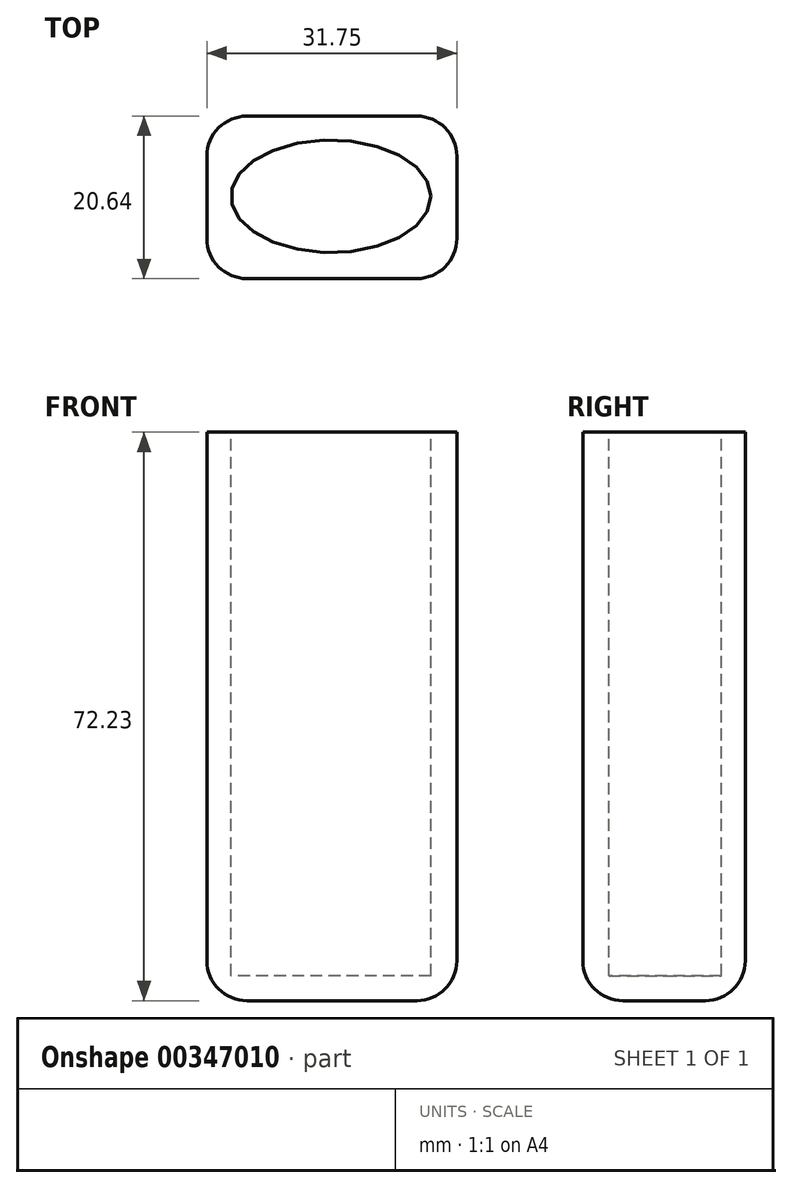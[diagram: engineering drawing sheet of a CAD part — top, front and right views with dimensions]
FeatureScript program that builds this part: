
annotation { "Feature Type Name" : "Feature", "Feature Type Description" : "" }
export const myFeature = defineFeature(function(context is Context, id is Id, definition is map)
    precondition{}
    {
        {
            var Q0;
            Q0=qCreatedBy(makeId("Top.planeOp"),FACE);
            var sketch = newSketch(context, id + "F0", { "sketchPlane" : qUnion([Q0])});
            skLineSegment(sketch, "E0.bottom", {"start": v(-12.58, 7.01) * mm, "end": v(12.82, 7.01) * mm});
            skLineSegment(sketch, "E0.top", {"start": v(-12.58, -7.27) * mm, "end": v(12.82, -7.27) * mm});
            skLineSegment(sketch, "E0.left", {"start": v(-12.58, 7.01) * mm, "end": v(-12.58, -7.27) * mm});
            skLineSegment(sketch, "E0.right", {"start": v(12.82, 7.01) * mm, "end": v(12.82, -7.27) * mm});
            skSolve(sketch);
        }
        {
            var Q0;
            Q0 = qSketchRegion(id + "F0", true);
            extrude(context, id + "F1", {"entities" : qUnion([Q0]), "depth" : 69.06 * mm});
        }
        {
            var Q0;
            Q0=makeQuery(id+"F1.opExtrude","SWEPT_FACE",FACE,{"disambiguationData":[OSD([sQuery(id+"F0.wireOp",EDGE,"E0.top")])]});
            extrude(context, id + "F2", {"entities" : qUnion([Q0]), "operationType" : NewBodyOperationType.ADD, "depth" : 3.17 * mm});
        }
        {
            var Q0;
            {var subQ0=sQuery(id+"F0.wireOp",EDGE,"E0.left");Q0=makeQuery(id+"F2.boolean.opBoolean","MERGE",FACE,{"derivedFrom":[makeQuery(id+"F1.opExtrude","SWEPT_FACE",FACE,{"disambiguationData":[OSD([subQ0])]}),makeQuery(id+"F2.opExtrude","SWEPT_FACE",FACE,{"disambiguationData":[OSD([sQuery(id+"F0.wireOp",EDGE,"E0.top"),subQ0])]})]});}
            extrude(context, id + "F3", {"entities" : qUnion([Q0]), "operationType" : NewBodyOperationType.ADD, "depth" : 3.17 * mm});
        }
        {
            var Q0;
            {var subQ0=sQuery(id+"F0.wireOp",EDGE,"E0.bottom");Q0=makeQuery(id+"F3.boolean.opBoolean","MERGE",FACE,{"derivedFrom":[makeQuery(id+"F1.opExtrude","SWEPT_FACE",FACE,{"disambiguationData":[OSD([subQ0])]}),makeQuery(id+"F3.opExtrude","SWEPT_FACE",FACE,{"disambiguationData":[OSD([subQ0,sQuery(id+"F0.wireOp",EDGE,"E0.left")])]})]});}
            extrude(context, id + "F4", {"entities" : qUnion([Q0]), "operationType" : NewBodyOperationType.ADD, "depth" : 3.17 * mm});
        }
        {
            var Q0;
            {var subQ0=sQuery(id+"F0.wireOp",EDGE,"E0.right");Q0=makeQuery(id+"F4.boolean.opBoolean","MERGE",FACE,{"derivedFrom":[makeQuery(id+"F2.boolean.opBoolean","MERGE",FACE,{"derivedFrom":[makeQuery(id+"F1.opExtrude","SWEPT_FACE",FACE,{"disambiguationData":[OSD([subQ0])]}),makeQuery(id+"F2.opExtrude","SWEPT_FACE",FACE,{"disambiguationData":[OSD([sQuery(id+"F0.wireOp",EDGE,"E0.top"),subQ0])]})]}),makeQuery(id+"F4.opExtrude","SWEPT_FACE",FACE,{"disambiguationData":[OSD([sQuery(id+"F0.wireOp",EDGE,"E0.bottom"),subQ0])]})]});}
            extrude(context, id + "F5", {"entities" : qUnion([Q0]), "operationType" : NewBodyOperationType.ADD, "depth" : 3.17 * mm});
        }
        {
            var Q0;
            {var subQ0=sQuery(id+"F0.wireOp",EDGE,"E0.right");var subQ1=sQuery(id+"F0.wireOp",EDGE,"E0.bottom");var subQ2=sQuery(id+"F0.wireOp",EDGE,"E0.top");var subQ3=sQuery(id+"F0.wireOp",EDGE,"E0.left");Q0=makeQuery(id+"F5.boolean.opBoolean","MERGE",FACE,{"derivedFrom":[makeQuery(id+"F4.boolean.opBoolean","MERGE",FACE,{"derivedFrom":[makeQuery(id+"F3.boolean.opBoolean","MERGE",FACE,{"derivedFrom":[makeQuery(id+"F2.boolean.opBoolean","MERGE",FACE,{"derivedFrom":[makeQuery(id+"F1.opExtrude","CAP_FACE",FACE,{"disambiguationData":[OSD([subQ1,subQ2,subQ3,subQ0])],"isStart":false}),makeQuery(id+"F2.opExtrude","SWEPT_FACE",FACE,{"disambiguationData":[OSD([subQ2]),TDD([makeQuery(id+"F1.opExtrude","CAP_EDGE",EDGE,{"disambiguationData":[OSD([subQ2])],"isStart":false})])]})]}),makeQuery(id+"F3.opExtrude","SWEPT_FACE",FACE,{"disambiguationData":[OSD([subQ2,subQ3]),TDD([makeQuery(id+"F2.boolean.opBoolean","MERGE",EDGE,{"derivedFrom":[makeQuery(id+"F1.opExtrude","CAP_EDGE",EDGE,{"disambiguationData":[OSD([subQ3])],"isStart":false}),makeQuery(id+"F2.opExtrude","SWEPT_EDGE",EDGE,{"disambiguationData":[OSD([subQ2,subQ3]),TDD([makeQuery(id+"F1.opExtrude","CAP_VERTEX",VERTEX,{"disambiguationData":[OSD([subQ2,subQ3])],"isStart":false})])]})]})])]})]}),makeQuery(id+"F4.opExtrude","SWEPT_FACE",FACE,{"disambiguationData":[OSD([subQ1,subQ3]),TDD([makeQuery(id+"F3.boolean.opBoolean","MERGE",EDGE,{"derivedFrom":[makeQuery(id+"F1.opExtrude","CAP_EDGE",EDGE,{"disambiguationData":[OSD([subQ1])],"isStart":false}),makeQuery(id+"F3.opExtrude","SWEPT_EDGE",EDGE,{"disambiguationData":[OSD([subQ1,subQ3]),TDD([makeQuery(id+"F1.opExtrude","CAP_VERTEX",VERTEX,{"disambiguationData":[OSD([subQ1,subQ3])],"isStart":false})])]})]})])]})]}),makeQuery(id+"F5.opExtrude","SWEPT_FACE",FACE,{"disambiguationData":[OSD([subQ1,subQ2,subQ0]),TDD([makeQuery(id+"F4.boolean.opBoolean","MERGE",EDGE,{"derivedFrom":[makeQuery(id+"F2.boolean.opBoolean","MERGE",EDGE,{"derivedFrom":[makeQuery(id+"F1.opExtrude","CAP_EDGE",EDGE,{"disambiguationData":[OSD([subQ0])],"isStart":false}),makeQuery(id+"F2.opExtrude","SWEPT_EDGE",EDGE,{"disambiguationData":[OSD([subQ2,subQ0]),TDD([makeQuery(id+"F1.opExtrude","CAP_VERTEX",VERTEX,{"disambiguationData":[OSD([subQ2,subQ0])],"isStart":false})])]})]}),makeQuery(id+"F4.opExtrude","SWEPT_EDGE",EDGE,{"disambiguationData":[OSD([subQ1,subQ0]),TDD([makeQuery(id+"F1.opExtrude","CAP_VERTEX",VERTEX,{"disambiguationData":[OSD([subQ1,subQ0])],"isStart":false})])]})]})])]})]});}
            var sketch = newSketch(context, id + "F6", { "sketchPlane" : qUnion([Q0])});
            skEllipse(sketch, "E1", {"center": v(0, 0) * mm, "majorRadius": 12.7 * mm, "minorRadius": 7.14 * mm, "majorAxis": v(1, 0)});
            skSolve(sketch);
        }
        {
            var Q0;
            Q0 = qSketchRegion(id + "F6", true);
            extrude(context, id + "F7", {"entities" : qUnion([Q0]), "operationType" : NewBodyOperationType.REMOVE, "oppositeDirection" : true, "depth" : 69.06 * mm});
        }
        {
            var Q0;
            {var subQ0=sQuery(id+"F0.wireOp",EDGE,"E0.right");var subQ1=sQuery(id+"F0.wireOp",EDGE,"E0.bottom");var subQ2=sQuery(id+"F0.wireOp",EDGE,"E0.top");var subQ3=sQuery(id+"F0.wireOp",EDGE,"E0.left");Q0=makeQuery(id+"F5.boolean.opBoolean","MERGE",FACE,{"derivedFrom":[makeQuery(id+"F4.boolean.opBoolean","MERGE",FACE,{"derivedFrom":[makeQuery(id+"F3.boolean.opBoolean","MERGE",FACE,{"derivedFrom":[makeQuery(id+"F2.boolean.opBoolean","MERGE",FACE,{"derivedFrom":[makeQuery(id+"F1.opExtrude","CAP_FACE",FACE,{"disambiguationData":[OSD([subQ1,subQ2,subQ3,subQ0])],"isStart":true}),makeQuery(id+"F2.opExtrude","SWEPT_FACE",FACE,{"disambiguationData":[OSD([subQ2]),TDD([makeQuery(id+"F1.opExtrude","CAP_EDGE",EDGE,{"disambiguationData":[OSD([subQ2])],"isStart":true})])]})]}),makeQuery(id+"F3.opExtrude","SWEPT_FACE",FACE,{"disambiguationData":[OSD([subQ2,subQ3]),TDD([makeQuery(id+"F2.boolean.opBoolean","MERGE",EDGE,{"derivedFrom":[makeQuery(id+"F1.opExtrude","CAP_EDGE",EDGE,{"disambiguationData":[OSD([subQ3])],"isStart":true}),makeQuery(id+"F2.opExtrude","SWEPT_EDGE",EDGE,{"disambiguationData":[OSD([subQ2,subQ3]),TDD([makeQuery(id+"F1.opExtrude","CAP_VERTEX",VERTEX,{"disambiguationData":[OSD([subQ2,subQ3])],"isStart":true})])]})]})])]})]}),makeQuery(id+"F4.opExtrude","SWEPT_FACE",FACE,{"disambiguationData":[OSD([subQ1,subQ3]),TDD([makeQuery(id+"F3.boolean.opBoolean","MERGE",EDGE,{"derivedFrom":[makeQuery(id+"F1.opExtrude","CAP_EDGE",EDGE,{"disambiguationData":[OSD([subQ1])],"isStart":true}),makeQuery(id+"F3.opExtrude","SWEPT_EDGE",EDGE,{"disambiguationData":[OSD([subQ1,subQ3]),TDD([makeQuery(id+"F1.opExtrude","CAP_VERTEX",VERTEX,{"disambiguationData":[OSD([subQ1,subQ3])],"isStart":true})])]})]})])]})]}),makeQuery(id+"F5.opExtrude","SWEPT_FACE",FACE,{"disambiguationData":[OSD([subQ1,subQ2,subQ0]),TDD([makeQuery(id+"F4.boolean.opBoolean","MERGE",EDGE,{"derivedFrom":[makeQuery(id+"F2.boolean.opBoolean","MERGE",EDGE,{"derivedFrom":[makeQuery(id+"F1.opExtrude","CAP_EDGE",EDGE,{"disambiguationData":[OSD([subQ0])],"isStart":true}),makeQuery(id+"F2.opExtrude","SWEPT_EDGE",EDGE,{"disambiguationData":[OSD([subQ2,subQ0]),TDD([makeQuery(id+"F1.opExtrude","CAP_VERTEX",VERTEX,{"disambiguationData":[OSD([subQ2,subQ0])],"isStart":true})])]})]}),makeQuery(id+"F4.opExtrude","SWEPT_EDGE",EDGE,{"disambiguationData":[OSD([subQ1,subQ0]),TDD([makeQuery(id+"F1.opExtrude","CAP_VERTEX",VERTEX,{"disambiguationData":[OSD([subQ1,subQ0])],"isStart":true})])]})]})])]})]});}
            var sketch = newSketch(context, id + "F8", { "sketchPlane" : qUnion([Q0])});
            skLineSegment(sketch, "E2.bottom", {"start": v(-15.75, 10.45) * mm, "end": v(16, 10.45) * mm});
            skLineSegment(sketch, "E2.top", {"start": v(-15.75, -10.19) * mm, "end": v(16, -10.19) * mm});
            skLineSegment(sketch, "E2.left", {"start": v(-15.75, 10.45) * mm, "end": v(-15.75, -10.19) * mm});
            skLineSegment(sketch, "E2.right", {"start": v(16, 10.45) * mm, "end": v(16, -10.19) * mm});
            skSolve(sketch);
        }
        {
            var Q0;
            Q0 = qSketchRegion(id + "F8", true);
            extrude(context, id + "F9", {"entities" : qUnion([Q0]), "operationType" : NewBodyOperationType.ADD, "depth" : 3.17 * mm});
        }
        {
            var Q0;
            {var subQ0=sQuery(id+"F0.wireOp",EDGE,"E0.left");var subQ1=sQuery(id+"F0.wireOp",EDGE,"E0.top");Q0=makeQuery(id+"F9.boolean.opBoolean","MERGE",EDGE,{"derivedFrom":[makeQuery(id+"F3.opExtrude","CAP_EDGE",EDGE,{"disambiguationData":[OSD([subQ1,subQ0]),TDD([makeQuery(id+"F2.opExtrude","CAP_EDGE",EDGE,{"disambiguationData":[OSD([subQ1,subQ0])],"isStart":false})])],"isStart":false}),makeQuery(id+"F9.opExtrude","SWEPT_EDGE",EDGE,{"disambiguationData":[OSD([sQuery(id+"F8.wireOp",EDGE,"E2.bottom"),sQuery(id+"F8.wireOp",EDGE,"E2.left")])]})]});}
            fillet(context, id + "F10", {"entities" : qUnion([Q0]), "radius" : 5.08 * mm, "tangentPropagation" : true, "allowEdgeOverflow" : false});
        }
        {
            var Q0;
            Q0=makeQuery(id+"F9.boolean.opBoolean","MERGE",EDGE,{"derivedFrom":[makeQuery(id+"F5.opExtrude","CAP_EDGE",EDGE,{"disambiguationData":[OSD([sQuery(id+"F0.wireOp",EDGE,"E0.top"),sQuery(id+"F0.wireOp",EDGE,"E0.right")])],"isStart":false}),makeQuery(id+"F9.opExtrude","SWEPT_EDGE",EDGE,{"disambiguationData":[OSD([sQuery(id+"F8.wireOp",EDGE,"E2.bottom"),sQuery(id+"F8.wireOp",EDGE,"E2.right")])]})]});
            fillet(context, id + "F11", {"entities" : qUnion([Q0]), "radius" : 5.08 * mm, "tangentPropagation" : true, "allowEdgeOverflow" : false});
        }
        {
            var Q0;
            Q0=makeQuery(id+"F9.boolean.opBoolean","MERGE",EDGE,{"derivedFrom":[makeQuery(id+"F5.opExtrude","CAP_EDGE",EDGE,{"disambiguationData":[OSD([sQuery(id+"F0.wireOp",EDGE,"E0.bottom"),sQuery(id+"F0.wireOp",EDGE,"E0.right")])],"isStart":false}),makeQuery(id+"F9.opExtrude","SWEPT_EDGE",EDGE,{"disambiguationData":[OSD([sQuery(id+"F8.wireOp",EDGE,"E2.top"),sQuery(id+"F8.wireOp",EDGE,"E2.right")])]})]});
            fillet(context, id + "F12", {"entities" : qUnion([Q0]), "radius" : 5.08 * mm, "tangentPropagation" : true, "allowEdgeOverflow" : false});
        }
        {
            var Q0;
            {var subQ0=sQuery(id+"F0.wireOp",EDGE,"E0.left");var subQ1=sQuery(id+"F0.wireOp",EDGE,"E0.bottom");Q0=makeQuery(id+"F9.boolean.opBoolean","MERGE",EDGE,{"derivedFrom":[makeQuery(id+"F4.opExtrude","CAP_EDGE",EDGE,{"disambiguationData":[OSD([subQ1,subQ0]),TDD([makeQuery(id+"F3.opExtrude","CAP_EDGE",EDGE,{"disambiguationData":[OSD([subQ1,subQ0])],"isStart":false})])],"isStart":false}),makeQuery(id+"F9.opExtrude","SWEPT_EDGE",EDGE,{"disambiguationData":[OSD([sQuery(id+"F8.wireOp",EDGE,"E2.top"),sQuery(id+"F8.wireOp",EDGE,"E2.left")])]})]});}
            var Q1;
            Q1=makeQuery(id+"F9.opExtrude","CAP_FACE",FACE,{"disambiguationData":[OSD([sQuery(id+"F8.wireOp",EDGE,"E2.bottom"),sQuery(id+"F8.wireOp",EDGE,"E2.top"),sQuery(id+"F8.wireOp",EDGE,"E2.left"),sQuery(id+"F8.wireOp",EDGE,"E2.right")])],"isStart":false});
            fillet(context, id + "F13", {"entities" : qUnion([Q0, Q1]), "radius" : 5.08 * mm, "tangentPropagation" : true, "allowEdgeOverflow" : false});
        }
    });
